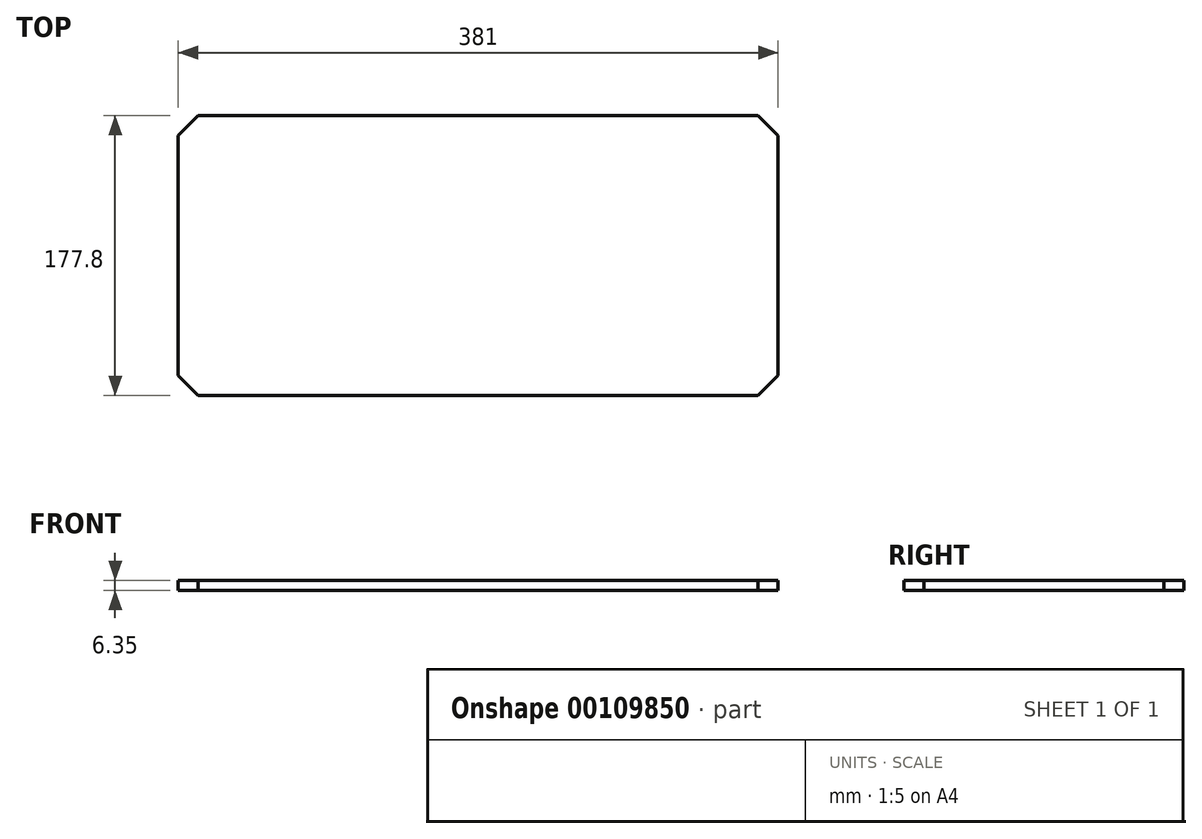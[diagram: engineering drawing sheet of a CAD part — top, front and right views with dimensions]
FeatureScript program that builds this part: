
annotation { "Feature Type Name" : "Feature", "Feature Type Description" : "" }
export const myFeature = defineFeature(function(context is Context, id is Id, definition is map)
    precondition{}
    {
        {
            var Q0;
            Q0=qCreatedBy(makeId("Top.planeOp"),FACE);
            var sketch = newSketch(context, id + "F0", { "sketchPlane" : qUnion([Q0])});
            skLineSegment(sketch, "E0.bottom", {"start": v(0, 0) * mm, "end": v(381, 0) * mm});
            skLineSegment(sketch, "E0.top", {"start": v(0, 177.8) * mm, "end": v(381, 177.8) * mm});
            skLineSegment(sketch, "E0.left", {"start": v(0, 0) * mm, "end": v(0, 177.8) * mm});
            skLineSegment(sketch, "E0.right", {"start": v(381, 0) * mm, "end": v(381, 177.8) * mm});
            skSolve(sketch);
        }
        {
            var Q0;
            Q0 = qSketchRegion(id + "F0", true);
            extrude(context, id + "F1", {"entities" : qUnion([Q0]), "depth" : 6.35 * mm});
        }
        {
            var Q0;
            Q0=makeQuery(id+"F1.opExtrude","SWEPT_EDGE",EDGE,{"disambiguationData":[OSD([sQuery(id+"F0.wireOp",EDGE,"E0.bottom"),sQuery(id+"F0.wireOp",EDGE,"E0.left")])]});
            var Q1;
            Q1=makeQuery(id+"F1.opExtrude","SWEPT_EDGE",EDGE,{"disambiguationData":[OSD([sQuery(id+"F0.wireOp",EDGE,"E0.top"),sQuery(id+"F0.wireOp",EDGE,"E0.left")])]});
            var Q2;
            Q2=makeQuery(id+"F1.opExtrude","SWEPT_EDGE",EDGE,{"disambiguationData":[OSD([sQuery(id+"F0.wireOp",EDGE,"E0.bottom"),sQuery(id+"F0.wireOp",EDGE,"E0.right")])]});
            var Q3;
            Q3=makeQuery(id+"F1.opExtrude","SWEPT_EDGE",EDGE,{"disambiguationData":[OSD([sQuery(id+"F0.wireOp",EDGE,"E0.top"),sQuery(id+"F0.wireOp",EDGE,"E0.right")])]});
            chamfer(context, id + "F2", {"entities" : qUnion([Q0, Q1, Q2, Q3]), "width" : 12.7 * mm, "tangentPropagation" : true});
        }
    });
